FCSTD DOCUMENT  (FreeCAD 0.20RUnknown)
Label: trackball_plate
License: All rights reserved
LicenseURL: http://en.wikipedia.org/wiki/All_rights_reserved
objects: Part::Part2DObjectPython×10, TechDraw::DrawViewDimension×10, Part::Feature×2, App::Part×1, Sketcher::SketchObject×1, App::DocumentObjectGroup×1, TechDraw::DrawSVGTemplate×1, TechDraw::DrawViewPart×1, TechDraw::DrawPage×1
note: 13 computed .brp shape members not serialized (recipe doc carries the construction recipe); baked Part::Feature solids carry a one-line shape summary decoded from their .brp

FEATURE [App::Part] Part  label="Faceplate"
  Origin = -> Origin
FEATURE [Sketcher::SketchObject] Sketch
  FullyConstrained = true
  MapMode = 2
  Support = -> [Part]
  sketch-geometry (73):
    g0: LineSegment StartX=0 StartY=0 StartZ=0 EndX=30.48 EndY=0 EndZ=0
    g1: LineSegment StartX=30.48 StartY=0 StartZ=0 EndX=30.48 EndY=-129 EndZ=0
    g2: LineSegment StartX=30.48 StartY=-129 StartZ=0 EndX=0 EndY=-129 EndZ=0
    g3: LineSegment StartX=0 StartY=-129 StartZ=0 EndX=0 EndY=0 EndZ=0
    g4: Circle CenterX=7.1 CenterY=-3.25 CenterZ=0 NormalX=0 NormalY=0 NormalZ=1 AngleXU=0 Radius=1.75
    g5: Circle CenterX=23.38 CenterY=-3.25 CenterZ=0 NormalX=0 NormalY=0 NormalZ=1 AngleXU=0 Radius=1.75
    g6: Circle CenterX=23.38 CenterY=-125.75 CenterZ=0 NormalX=0 NormalY=0 NormalZ=1 AngleXU=0 Radius=1.75
    g7: Circle CenterX=7.74 CenterY=-49 CenterZ=0 NormalX=0 NormalY=0 NormalZ=1 AngleXU=0 Radius=1.4
    g8: Circle CenterX=22.74 CenterY=-49 CenterZ=0 NormalX=0 NormalY=0 NormalZ=1 AngleXU=0 Radius=1.4
    g9: ArcOfCircle CenterX=11.565 CenterY=-46.825 CenterZ=0 NormalX=0 NormalY=0 NormalZ=1 AngleXU=0 Radius=1.2 StartAngle=1.5708 EndAngle=3.14159
    g10: LineSegment StartX=11.565 StartY=-45.625 StartZ=0 EndX=18.915 EndY=-45.625 EndZ=0
    g11: ArcOfCircle CenterX=18.915 CenterY=-46.825 CenterZ=0 NormalX=0 NormalY=0 NormalZ=1 AngleXU=0 Radius=1.2 StartAngle=2.6e-15 EndAngle=1.5708
    g12: LineSegment StartX=20.115 StartY=-46.825 StartZ=0 EndX=20.115 EndY=-51.175 EndZ=0
    g13: ArcOfCircle CenterX=18.915 CenterY=-51.175 CenterZ=0 NormalX=0 NormalY=0 NormalZ=1 AngleXU=0 Radius=1.2 StartAngle=4.71239 EndAngle=6.28319
    g14: LineSegment StartX=18.915 StartY=-52.375 StartZ=0 EndX=11.565 EndY=-52.375 EndZ=0
    g15: ArcOfCircle CenterX=11.565 CenterY=-51.175 CenterZ=0 NormalX=0 NormalY=0 NormalZ=1 AngleXU=0 Radius=1.2 StartAngle=3.14159 EndAngle=4.71239
    g16: LineSegment StartX=10.365 StartY=-51.175 StartZ=0 EndX=10.365 EndY=-46.825 EndZ=0
    g17: GeomPoint X=10.365 Y=-45.625 Z=0
    g18: GeomPoint X=20.115 Y=-52.375 Z=0
    g19: LineSegment StartX=0 StartY=-49 StartZ=0 EndX=7.74 EndY=-49 EndZ=0
    g20: LineSegment StartX=22.74 StartY=-49 StartZ=0 EndX=30.48 EndY=-49 EndZ=0
    g21: LineSegment StartX=10.365 StartY=-49 StartZ=0 EndX=15.24 EndY=-49 EndZ=0
    g22: LineSegment StartX=15.24 StartY=-49 StartZ=0 EndX=20.115 EndY=-49 EndZ=0
    g23: LineSegment StartX=15.24 StartY=-45.625 StartZ=0 EndX=15.24 EndY=-49 EndZ=0
    g24: LineSegment StartX=15.24 StartY=-49 StartZ=0 EndX=15.24 EndY=-52.375 EndZ=0
    g25: LineSegment StartX=7.74 StartY=-49 StartZ=0 EndX=10.365 EndY=-49 EndZ=0
    g26: LineSegment StartX=20.115 StartY=-49 StartZ=0 EndX=22.74 EndY=-49 EndZ=0
    g27: Circle CenterX=15.24 CenterY=-13.94 CenterZ=0 NormalX=0 NormalY=0 NormalZ=1 AngleXU=0 Radius=1.6
    g28: Circle CenterX=15.24 CenterY=-39.06 CenterZ=0 NormalX=0 NormalY=0 NormalZ=1 AngleXU=0 Radius=1.6
    g29: ArcOfCircle CenterX=12.49 CenterY=-19.25 CenterZ=0 NormalX=0 NormalY=0 NormalZ=1 AngleXU=0 Radius=2 StartAngle=1.41303 EndAngle=3.14159
    g30: ArcOfCircle CenterX=12.49 CenterY=-33.75 CenterZ=0 NormalX=0 NormalY=0 NormalZ=1 AngleXU=0 Radius=2 StartAngle=3.14159 EndAngle=4.87016
    g31: ArcOfCircle CenterX=17.99 CenterY=-20.125 CenterZ=0 NormalX=0 NormalY=0 NormalZ=1 AngleXU=0 Radius=2 StartAngle=4e-16 EndAngle=1.41303
    g32: ArcOfCircle CenterX=17.99 CenterY=-32.875 CenterZ=0 NormalX=0 NormalY=0 NormalZ=1 AngleXU=0 Radius=2 StartAngle=4.87016 EndAngle=6.28319
    g33: LineSegment StartX=12.8042 StartY=-17.2748 StartZ=0 EndX=18.3042 EndY=-18.1498 EndZ=0
    g34: LineSegment StartX=12.8042 StartY=-35.7252 StartZ=0 EndX=18.3042 EndY=-34.8502 EndZ=0
    g35: LineSegment StartX=15.24 StartY=-13.94 StartZ=0 EndX=15.24 EndY=-26.5 EndZ=0
    g36: LineSegment StartX=15.24 StartY=-26.5 StartZ=0 EndX=15.24 EndY=-39.06 EndZ=0
    g37: LineSegment StartX=10.49 StartY=-19.25 StartZ=0 EndX=10.49 EndY=-26.5 EndZ=0
    g38: LineSegment StartX=10.49 StartY=-26.5 StartZ=0 EndX=10.49 EndY=-33.75 EndZ=0
    g39: LineSegment StartX=19.99 StartY=-20.125 StartZ=0 EndX=19.99 EndY=-26.5 EndZ=0
    g40: LineSegment StartX=19.99 StartY=-26.5 StartZ=0 EndX=19.99 EndY=-32.875 EndZ=0
    g41: LineSegment StartX=15.24 StartY=-26.5 StartZ=0 EndX=10.49 EndY=-26.5 EndZ=0
    g42: LineSegment StartX=19.99 StartY=-26.5 StartZ=0 EndX=15.24 EndY=-26.5 EndZ=0
    g43: LineSegment StartX=8.99 StartY=-11 StartZ=0 EndX=21.49 EndY=-11 EndZ=0
    g44: LineSegment StartX=21.49 StartY=-11 StartZ=0 EndX=21.49 EndY=-42 EndZ=0
    g45: LineSegment StartX=21.49 StartY=-42 StartZ=0 EndX=8.99 EndY=-42 EndZ=0
    g46: LineSegment StartX=8.99 StartY=-42 StartZ=0 EndX=8.99 EndY=-11 EndZ=0
    g47: LineSegment StartX=15.24 StartY=-13.94 StartZ=0 EndX=15.24 EndY=-11 EndZ=0
    g48: LineSegment StartX=15.24 StartY=-39.06 StartZ=0 EndX=15.24 EndY=-42 EndZ=0
    g49: LineSegment StartX=10.49 StartY=-26.5 StartZ=0 EndX=8.99 EndY=-26.5 EndZ=0
    g50: LineSegment StartX=19.99 StartY=-26.5 StartZ=0 EndX=21.49 EndY=-26.5 EndZ=0
    g51: LineSegment StartX=5.295 StartY=-44 StartZ=0 EndX=25.185 EndY=-44 EndZ=0
    g52: LineSegment StartX=25.185 StartY=-44 StartZ=0 EndX=25.185 EndY=-54 EndZ=0
    g53: LineSegment StartX=25.185 StartY=-54 StartZ=0 EndX=5.295 EndY=-54 EndZ=0
    g54: LineSegment StartX=5.295 StartY=-54 StartZ=0 EndX=5.295 EndY=-44 EndZ=0
    g55: LineSegment StartX=15.24 StartY=-52.375 StartZ=0 EndX=15.24 EndY=-54 EndZ=0
    g56: LineSegment StartX=15.24 StartY=-45.625 StartZ=0 EndX=15.24 EndY=-44 EndZ=0
    g57: LineSegment StartX=0 StartY=-44 StartZ=0 EndX=5.295 EndY=-44 EndZ=0
    g58: LineSegment StartX=25.185 StartY=-44 StartZ=0 EndX=30.48 EndY=-44 EndZ=0
    g59: LineSegment StartX=4.74 StartY=-56 StartZ=0 EndX=25.74 EndY=-56 EndZ=0
    g60: LineSegment StartX=25.74 StartY=-56 StartZ=0 EndX=25.74 EndY=-109 EndZ=0
    g61: LineSegment StartX=25.74 StartY=-109 StartZ=0 EndX=4.74 EndY=-109 EndZ=0
    g62: LineSegment StartX=4.74 StartY=-109 StartZ=0 EndX=4.74 EndY=-56 EndZ=0
    g63: LineSegment StartX=4.74 StartY=-56 StartZ=0 EndX=0 EndY=-56 EndZ=0
    g64: LineSegment StartX=25.74 StartY=-56 StartZ=0 EndX=30.48 EndY=-56 EndZ=0
    g65: LineSegment StartX=16.48 StartY=-110.8 StartZ=0 EndX=21.48 EndY=-110.8 EndZ=0
    g66: LineSegment StartX=21.48 StartY=-110.8 StartZ=0 EndX=21.48 EndY=-119 EndZ=0
    g67: LineSegment StartX=21.48 StartY=-119 StartZ=0 EndX=16.48 EndY=-119 EndZ=0
    g68: LineSegment StartX=16.48 StartY=-119 StartZ=0 EndX=16.48 EndY=-110.8 EndZ=0
    g69: Circle CenterX=7.1 CenterY=-125.75 CenterZ=0 NormalX=0 NormalY=0 NormalZ=1 AngleXU=0 Radius=1.75
    g70: Circle CenterX=18.98 CenterY=-114.9 CenterZ=0 NormalX=0 NormalY=0 NormalZ=1 AngleXU=0 Radius=2.5
    g71: LineSegment StartX=16.48 StartY=-119 StartZ=0 EndX=21.48 EndY=-110.8 EndZ=0
    g72: LineSegment StartX=16.48 StartY=-110.8 StartZ=0 EndX=21.48 EndY=-119 EndZ=0
  constraints (202):
    c: Coincident(g0,g1)
    c: Coincident(g1,g2)
    c: Coincident(g2,g3)
    c: Coincident(g3,g0)
    c: Horizontal(g0)
    c: Horizontal(g2)
    c: Vertical(g1)
    c: Vertical(g3)
    c: DistanceX(g0,g0) = 30.48
    c: DistanceY(g3,g3) = 129  'Faceplate height'
    c: Coincident(g-1,g0)
    c: Diameter(g4) = 3.5
    c: Diameter(g5) = 3.5
    c: Diameter(g6) = 3.5
    c: Horizontal(g4,g5)
    c: Vertical(g5,g6)
    c: Distance(g5,g0) = 3.25
    c: Distance(g5,g1) = 7.1
    c: Distance(g4,g3) = 7.1
    c: Diameter(g7) = 2.8
    c: Diameter(g8) = 2.8
    c: Horizontal(g7,g8)
    c: Distance(g7,g8) = 15
    c: Tangent(g9,g10) = 1.5708
    c: Tangent(g10,g11) = 1.5708
    c: Tangent(g11,g12) = 1.5708
    c: Tangent(g12,g13) = 1.5708
    c: Tangent(g13,g14) = 1.5708
    c: Tangent(g14,g15) = 1.5708
    c: Tangent(g15,g16) = 1.5708
    c: Tangent(g16,g9) = 1.5708
    c: Horizontal(g10)
    c: Horizontal(g14)
    c: Vertical(g12)
    c: Vertical(g16)
    c: Equal(g9,g11)
    c: Equal(g11,g13)
    c: Equal(g13,g15)
    c: PointOnObject(g17,g10)
    c: PointOnObject(g17,g16)
    c: PointOnObject(g18,g12)
    c: PointOnObject(g18,g14)
    c: DistanceX(g9,g11) = 9.75
    c: DistanceY(g14,g9) = 6.75
    c: DistanceX(g9,g9) = 1.2
    c: PointOnObject(g19,g3)
    c: Coincident(g19,g7)
    c: Coincident(g20,g8)
    c: PointOnObject(g20,g1)
    c: Horizontal(g20)
    c: Equal(g19,g20)
    c: PointOnObject(g23,g10)
    c: PointOnObject(g24,g14)
    c: PointOnObject(g21,g16)
    c: PointOnObject(g22,g12)
    c: Coincident(g21,g22)
    c: Horizontal(g21)
    c: Horizontal(g22)
    c: Coincident(g23,g24)
    c: Vertical(g23)
    c: Vertical(g24)
    c: Coincident(g21,g23)
    c: Equal(g21,g22)
    c: Equal(g23,g24)
    c: Coincident(g25,g7)
    c: Coincident(g25,g21)
    c: Coincident(g26,g22)
    c: Coincident(g26,g8)
    c: Horizontal(g25)
    c: Equal(g25,g26)
    c: Diameter(g27) = 3.2
    c: Diameter(g28) = 3.2
    c: DistanceY(g28,g27) = 25.12
    c: Diameter(g29) = 4
    c: Diameter(g31) = 4
    c: Diameter(g30) = 4
    c: Diameter(g32) = 4
    c: Vertical(g31,g32)
    c: Vertical(g29,g30)
    c: DistanceX(g29,g31) = 5.5
    c: DistanceY(g32,g31) = 12.75
    c: DistanceY(g30,g29) = 14.5
    c: Tangent(g31,g33) = 1.5708
    c: Tangent(g31,g39) = 1.5708
    c: Tangent(g29,g37) = -1.5708
    c: Tangent(g29,g33) = 1.5708
    c: Tangent(g30,g34) = -1.5708
    c: Tangent(g30,g38) = -1.5708
    c: Tangent(g32,g40) = 1.5708
    c: Tangent(g32,g34) = -1.5708
    c: Coincident(g35,g27)
    c: Coincident(g36,g28)
    c: Coincident(g35,g36)
    c: Vertical(g35)
    c: Vertical(g36)
    c: Equal(g35,g36)
    c: Coincident(g37,g38)
    c: Vertical(g37)
    c: Equal(g37,g38)
    c: Coincident(g39,g40)
    c: Equal(g40,g39)
    c: Coincident(g41,g35)
    c: Coincident(g41,g37)
    c: Coincident(g42,g39)
    c: Coincident(g42,g35)
    c: Equal(g41,g42)
    c: Horizontal(g41)
    c: Horizontal(g42)
    c: Vertical(g39)
    c: Horizontal(g19)
    c: Vertical(g28,g23)
    c: Coincident(g43,g44)
    c: Coincident(g44,g45)
    c: Coincident(g45,g46)
    c: Coincident(g46,g43)
    c: Horizontal(g43)
    c: Horizontal(g45)
    c: Vertical(g44)
    c: Vertical(g46)
    c: DistanceX(g43,g43) = 12.5
    c: DistanceY(g44,g44) = 31
    c: Coincident(g47,g27)
    c: PointOnObject(g47,g43)
    c: Coincident(g48,g28)
    c: PointOnObject(g48,g45)
    c: Coincident(g49,g37)
    c: PointOnObject(g49,g46)
    c: Coincident(g50,g39)
    c: PointOnObject(g50,g44)
    c: Vertical(g47)
    c: Vertical(g48)
    c: Horizontal(g49)
    c: Horizontal(g50)
    c: Equal(g49,g50)
    c: Equal(g47,g48)
    c: DistanceY(g47,g0) = 11
    c: Coincident(g51,g52)
    c: Coincident(g52,g53)
    c: Coincident(g53,g54)
    c: Coincident(g54,g51)
    c: Horizontal(g51)
    c: Horizontal(g53)
    c: Vertical(g52)
    c: Vertical(g54)
    c: DistanceX(g51,g51) = 19.89
    c: DistanceY(g52,g52) = 10
    c: Coincident(g55,g24)
    c: PointOnObject(g55,g53)
    c: Coincident(g56,g23)
    c: PointOnObject(g56,g51)
    c: Vertical(g56)
    c: Vertical(g55)
    c: Equal(g55,g56)
    c: PointOnObject(g57,g3)
    c: Coincident(g57,g51)
    c: Horizontal(g57)
    c: Coincident(g58,g51)
    c: PointOnObject(g58,g1)
    c: Equal(g57,g58)
    c: Horizontal(g58)
    c: DistanceY(g51,g45) = 2
    c: Coincident(g59,g60)
    c: Coincident(g60,g61)
    c: Coincident(g61,g62)
    c: Coincident(g62,g59)
    c: Horizontal(g59)
    c: Horizontal(g61)
    c: Vertical(g60)
    c: Vertical(g62)
    c: DistanceX(g59,g59) = 21
    c: DistanceY(g60,g60) = 53
    c: Coincident(g63,g59)
    c: PointOnObject(g63,g3)
    c: Coincident(g64,g59)
    c: PointOnObject(g64,g1)
    c: Equal(g64,g63)
    c: Horizontal(g63)
    c: Horizontal(g64)
    c: DistanceY(g59,g53) = 2
    c: Coincident(g65,g66)
    c: Coincident(g66,g67)
    c: Coincident(g67,g68)
    c: Coincident(g68,g65)
    c: Horizontal(g65)
    c: Horizontal(g67)
    c: Vertical(g66)
    c: Vertical(g68)
    c: DistanceY(g66,g66) = 8.2
    c: DistanceX(g65,g65) = 5
    c: Horizontal(g69,g6)
    c: Diameter(g69) = 3.5
    c: Vertical(g69,g4)
    c: DistanceY(g1,g6) = 3.25
    c: Coincident(g71,g67)
    c: Coincident(g71,g65)
    c: Coincident(g72,g65)
    c: Coincident(g72,g66)
    c: PointOnObject(g70,g72)
    c: PointOnObject(g70,g71)
    c: DistanceY(g1,g66) = 10
    c: Diameter(g70) = 5
    c: DistanceX(g66,g1) = 9
FEATURE [Part::Part2DObjectPython] Wire  # Draft 2D object (typed FeaturePython)
  Area = 0
  ChamferSize = 0
  Closed = true
  End = (0,-129,0)
  FilletRadius = 0
  Length = 318.96
  MakeFace = false
  Points = (4) [(0,0,0),(30.48,0,0),(30.48,-129,0),(0,-129,0)]
  Start = (0,0,0)
  Subdivisions = 0
FEATURE [Part::Part2DObjectPython] Circle  # Draft 2D object (typed FeaturePython)
  Area = 0
  FirstAngle = 0
  LastAngle = 0
  MakeFace = false
  Placement = pos=(7.1,-3.25,0) rot=(0,0,1;0rad)
  Radius = 1.75
FEATURE [Part::Part2DObjectPython] Circle001  # Draft 2D object (typed FeaturePython)
  Area = 0
  FirstAngle = 0
  LastAngle = 0
  MakeFace = false
  Placement = pos=(23.38,-3.25,0) rot=(0,0,1;0rad)
  Radius = 1.75
FEATURE [Part::Part2DObjectPython] Circle002  # Draft 2D object (typed FeaturePython)
  Area = 0
  FirstAngle = 0
  LastAngle = 0
  MakeFace = false
  Placement = pos=(23.38,-125.75,0) rot=(0,0,1;0rad)
  Radius = 1.75
FEATURE [Part::Part2DObjectPython] Circle003  # Draft 2D object (typed FeaturePython)
  Area = 0
  FirstAngle = 0
  LastAngle = 0
  MakeFace = false
  Placement = pos=(7.74,-49,0) rot=(0,0,1;0rad)
  Radius = 1.4
FEATURE [Part::Part2DObjectPython] Circle004  # Draft 2D object (typed FeaturePython)
  Area = 0
  FirstAngle = 0
  LastAngle = 0
  MakeFace = false
  Placement = pos=(22.74,-49,0) rot=(0,0,1;0rad)
  Radius = 1.4
FEATURE [Part::Feature] Sketch001
  shape: bbox 9.75 x 6.75 x 2e-07 mm, 0 faces, 0 solids (baked)
FEATURE [Part::Part2DObjectPython] Circle005  # Draft 2D object (typed FeaturePython)
  Area = 0
  FirstAngle = 0
  LastAngle = 0
  MakeFace = false
  Placement = pos=(15.24,-13.94,0) rot=(0,0,1;0rad)
  Radius = 1.6
FEATURE [Part::Part2DObjectPython] Circle006  # Draft 2D object (typed FeaturePython)
  Area = 0
  FirstAngle = 0
  LastAngle = 0
  MakeFace = false
  Placement = pos=(15.24,-39.06,0) rot=(0,0,1;0rad)
  Radius = 1.6
FEATURE [Part::Feature] Sketch002
  shape: bbox 6.77 x 15.29 x 2e-07 mm, 0 faces, 0 solids (baked)
FEATURE [Part::Part2DObjectPython] Circle007  # Draft 2D object (typed FeaturePython)
  Area = 0
  FirstAngle = 0
  LastAngle = 0
  MakeFace = false
  Placement = pos=(7.1,-125.75,0) rot=(0,0,1;0rad)
  Radius = 1.75
FEATURE [Part::Part2DObjectPython] Circle008  # Draft 2D object (typed FeaturePython)
  Area = 0
  FirstAngle = 0
  LastAngle = 0
  MakeFace = false
  Placement = pos=(18.98,-114.9,0) rot=(0,0,1;0rad)
  Radius = 2.5
FEATURE [App::DocumentObjectGroup] Group  label="draft"
  Group = -> [Wire,Circle,Circle001,Circle002,Circle003,Circle004,Sketch001,Circle005,Circle006,Sketch002,Circle007,Circle008]
FEATURE [TechDraw::DrawSVGTemplate] Template
  EditableTexts = Designed_by_Name=Designed by Name; Drawing_number=Drawing number; FC-Date=Date; FC-SC=Scale; FC-SH=Sheet; FC-Title=Title; Subtitle=Subtitle; Weight=Weight
  Height = 210
  Orientation = 1
  Width = 297
FEATURE [TechDraw::DrawViewPart] View  label="Front"
  Caption = Front
  CoarseView = false
  Direction = (0,0,1)
  Focus = 100
  HardHidden = false
  IsoCount = 0
  IsoHidden = false
  IsoVisible = false
  LockPosition = false
  Perspective = false
  Rotation = 0
  Scale = 1.25
  ScaleType = 0
  SeamHidden = false
  SeamVisible = true
  SmoothHidden = false
  SmoothVisible = true
  Source = -> [Group]
  X = 52.9737
  XDirection = (1,0,0)
  Y = 105
FEATURE [TechDraw::DrawViewDimension] Dimension
  AngleOverride = false
  Arbitrary = false
  ArbitraryTolerances = false
  EqualTolerance = true
  ExtensionAngle = 0
  FormatSpec = %.2w
  FormatSpecOverTolerance = %+.2w
  FormatSpecUnderTolerance = %+.2w
  Inverted = false
  LineAngle = 0
  LockPosition = false
  MeasureType = 1
  OverTolerance = 0
  References2D = -> [View]
  Rotation = 0
  Scale = 1.25
  ScaleType = 0
  TheoreticalExact = false
  Type = 1
  UnderTolerance = 0
  X = 0
  Y = 95.2237
FEATURE [TechDraw::DrawViewDimension] Dimension001
  AngleOverride = false
  Arbitrary = false
  ArbitraryTolerances = false
  EqualTolerance = true
  ExtensionAngle = 0
  FormatSpec = %.2w
  FormatSpecOverTolerance = %+.2w
  FormatSpecUnderTolerance = %+.2w
  Inverted = false
  LineAngle = 0
  LockPosition = false
  MeasureType = 1
  OverTolerance = 0
  References2D = -> [View]
  Rotation = 0
  Scale = 1.25
  ScaleType = 0
  TheoreticalExact = false
  Type = 2
  UnderTolerance = 0
  X = -32.0163
  Y = 2.5
FEATURE [TechDraw::DrawViewDimension] Dimension002
  AngleOverride = false
  Arbitrary = false
  ArbitraryTolerances = false
  EqualTolerance = true
  ExtensionAngle = 0
  FormatSpec = ⌀%.2w
  FormatSpecOverTolerance = %+.2w
  FormatSpecUnderTolerance = %+.2w
  Inverted = false
  LineAngle = 0
  LockPosition = false
  MeasureType = 1
  OverTolerance = 0
  References2D = -> [View]
  Rotation = 0
  Scale = 1.25
  ScaleType = 0
  TheoreticalExact = false
  Type = 5
  UnderTolerance = 0
  X = 10.6579
  Y = -54.6711
FEATURE [TechDraw::DrawViewDimension] Dimension003
  AngleOverride = false
  Arbitrary = false
  ArbitraryTolerances = false
  EqualTolerance = true
  ExtensionAngle = 0
  FormatSpec = ⌀%.2w
  FormatSpecOverTolerance = %+.2w
  FormatSpecUnderTolerance = %+.2w
  Inverted = false
  LineAngle = 0
  LockPosition = false
  MeasureType = 1
  OverTolerance = 0
  References2D = -> [View]
  Rotation = 0
  Scale = 1.25
  ScaleType = 0
  TheoreticalExact = false
  Type = 5
  UnderTolerance = 0
  X = 27.6316
  Y = 69.2763
FEATURE [TechDraw::DrawViewDimension] Dimension005
  AngleOverride = false
  Arbitrary = false
  ArbitraryTolerances = false
  EqualTolerance = true
  ExtensionAngle = 0
  FormatSpec = ⌀%.2w
  FormatSpecOverTolerance = %+.2w
  FormatSpecUnderTolerance = %+.2w
  Inverted = false
  LineAngle = 0
  LockPosition = false
  MeasureType = 1
  OverTolerance = 0
  References2D = -> [View]
  Rotation = 0
  Scale = 1.25
  ScaleType = 0
  TheoreticalExact = false
  Type = 5
  UnderTolerance = 0
  X = -8.68421
  Y = 33.3553
FEATURE [TechDraw::DrawViewDimension] Dimension006
  AngleOverride = false
  Arbitrary = false
  ArbitraryTolerances = false
  EqualTolerance = true
  ExtensionAngle = 0
  FormatSpec = ⌀%.2w
  FormatSpecOverTolerance = %+.2w
  FormatSpecUnderTolerance = %+.2w
  Inverted = false
  LineAngle = 0
  LockPosition = false
  MeasureType = 1
  OverTolerance = 0
  References2D = -> [View]
  Rotation = 0
  Scale = 1.25
  ScaleType = 0
  TheoreticalExact = false
  Type = 5
  UnderTolerance = 0
  X = 0
  Y = -70.8553
FEATURE [TechDraw::DrawViewDimension] Dimension007
  AngleOverride = false
  Arbitrary = false
  ArbitraryTolerances = false
  EqualTolerance = true
  ExtensionAngle = 0
  FormatSpec = %.2w
  FormatSpecOverTolerance = %+.2w
  FormatSpecUnderTolerance = %+.2w
  Inverted = false
  LineAngle = 0
  LockPosition = false
  MeasureType = 1
  OverTolerance = 0
  References2D = -> [View]
  Rotation = 0
  Scale = 1.25
  ScaleType = 0
  TheoreticalExact = false
  Type = 1
  UnderTolerance = 0
  X = -9e-16
  Y = 50
FEATURE [TechDraw::DrawViewDimension] Dimension008
  AngleOverride = false
  Arbitrary = false
  ArbitraryTolerances = false
  EqualTolerance = true
  ExtensionAngle = 0
  FormatSpec = %.2w
  FormatSpecOverTolerance = %+.2w
  FormatSpecUnderTolerance = %+.2w
  Inverted = false
  LineAngle = 0
  LockPosition = false
  MeasureType = 1
  OverTolerance = 0
  References2D = -> [View]
  Rotation = 0
  Scale = 1.25
  ScaleType = 0
  TheoreticalExact = false
  Type = 1
  UnderTolerance = 0
  X = 0
  Y = 89.6711
FEATURE [TechDraw::DrawViewDimension] Dimension009
  AngleOverride = false
  Arbitrary = false
  ArbitraryTolerances = false
  EqualTolerance = true
  ExtensionAngle = 0
  FormatSpec = %.2w
  FormatSpecOverTolerance = %+.2w
  FormatSpecUnderTolerance = %+.2w
  Inverted = false
  LineAngle = 0
  LockPosition = false
  MeasureType = 1
  OverTolerance = 0
  References2D = -> [View]
  Rotation = 0
  Scale = 1.25
  ScaleType = 0
  TheoreticalExact = false
  Type = 2
  UnderTolerance = 0
  X = -24.9227
  Y = 36.0855
FEATURE [TechDraw::DrawViewDimension] Dimension010
  AngleOverride = false
  Arbitrary = false
  ArbitraryTolerances = false
  EqualTolerance = true
  ExtensionAngle = 0
  FormatSpec = %.2w
  FormatSpecOverTolerance = %+.2w
  FormatSpecUnderTolerance = %+.2w
  Inverted = false
  LineAngle = 0
  LockPosition = false
  MeasureType = 1
  OverTolerance = 0
  References2D = -> [View]
  Rotation = 0
  Scale = 1.25
  ScaleType = 0
  TheoreticalExact = false
  Type = 1
  UnderTolerance = 0
  X = 0
  Y = 12.8405
FEATURE [TechDraw::DrawPage] Page
  KeepUpdated = true
  NextBalloonIndex = 1
  ProjectionType = 0
  Scale = 1.25
  Template = -> Template
  Views = -> [View,Dimension,Dimension001,Dimension002,Dimension003,Dimension005,Dimension006,Dimension007,Dimension008,Dimension009,Dimension010]
